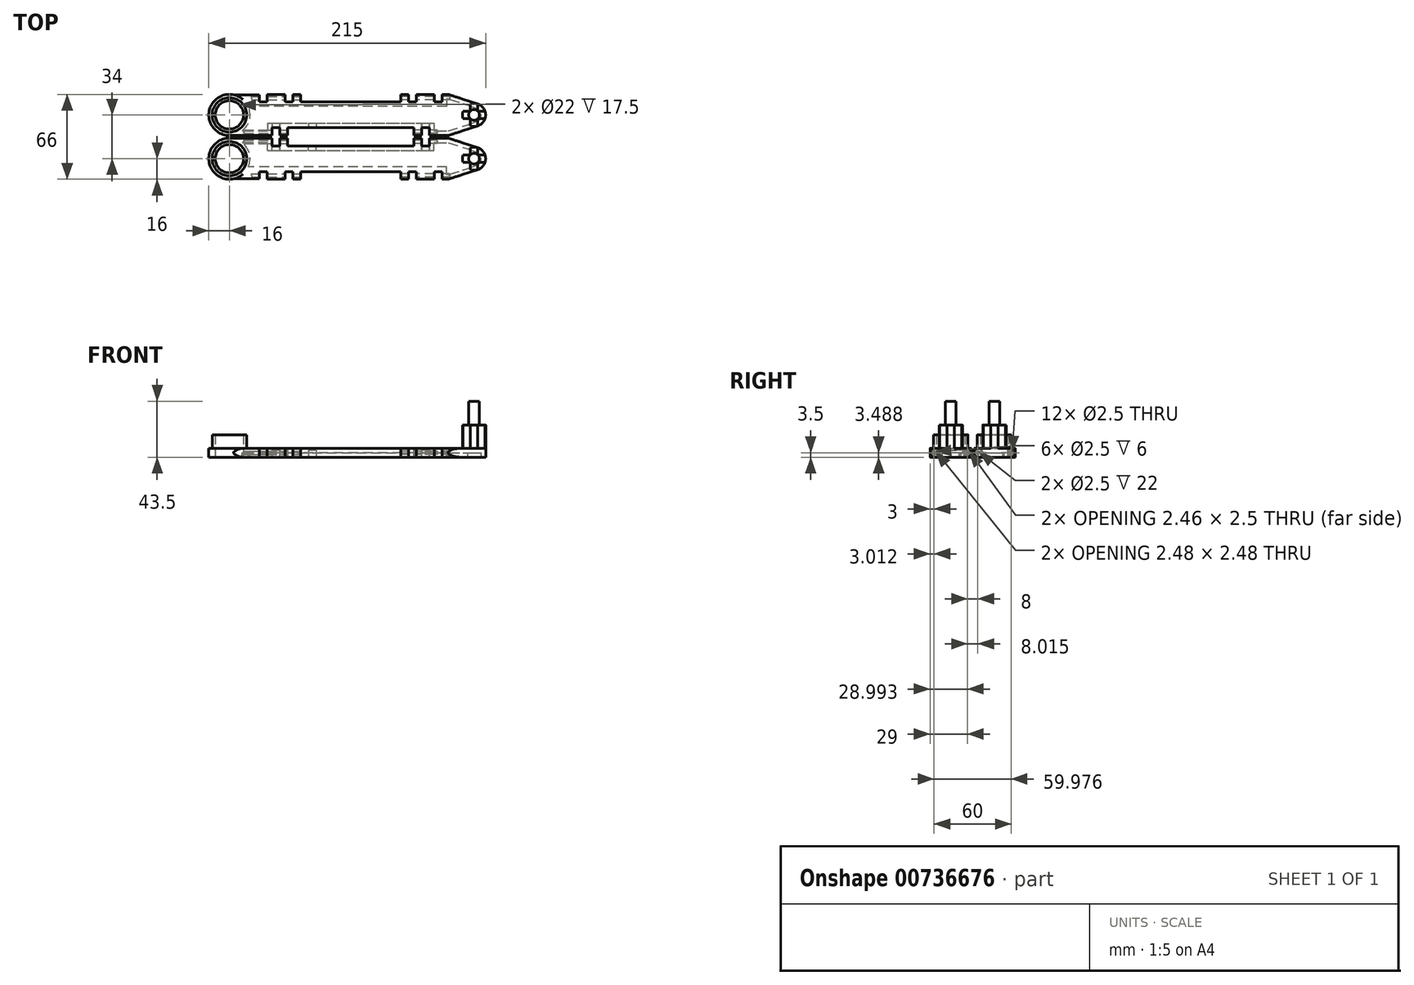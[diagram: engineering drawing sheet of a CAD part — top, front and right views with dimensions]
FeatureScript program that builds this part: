
annotation { "Feature Type Name" : "Feature", "Feature Type Description" : "" }
export const myFeature = defineFeature(function(context is Context, id is Id, definition is map)
    precondition{}
    {
        {
            var Q0;
            Q0=qCreatedBy(makeId("Top.planeOp"),FACE);
            var sketch = newSketch(context, id + "F0", { "sketchPlane" : qUnion([Q0])});
            skCircle(sketch, "E0", {"center": v(-95, 0) * mm, "radius": 11 * mm});
            skCircle(sketch, "E1", {"center": v(95, 0) * mm, "radius": 4.15 * mm});
            skCircle(sketch, "E2", {"center": v(95, 0) * mm, "radius": 9 * mm});
            skCircle(sketch, "E3", {"center": v(-95, 0) * mm, "radius": 16 * mm});
            skLineSegment(sketch, "E4.top", {"start": v(-71.75, 10) * mm, "end": v(-65.75, 10) * mm});
            skLineSegment(sketch, "E4.left", {"start": v(-71.75, 15.67) * mm, "end": v(-71.75, 10) * mm});
            skLineSegment(sketch, "E4.right", {"start": v(-65.75, 16) * mm, "end": v(-65.75, 10) * mm});
            skLineSegment(sketch, "E5.top", {"start": v(-51.75, 10) * mm, "end": v(-45.75, 10) * mm});
            skLineSegment(sketch, "E5.left", {"start": v(-51.75, 16) * mm, "end": v(-51.75, 10) * mm});
            skLineSegment(sketch, "E5.right", {"start": v(-45.75, 16) * mm, "end": v(-45.75, 10) * mm});
            skLineSegment(sketch, "E6.bottom", {"start": v(50.25, 16) * mm, "end": v(64.25, 16) * mm});
            skLineSegment(sketch, "E6.left", {"start": v(50.25, 16) * mm, "end": v(50.25, 10) * mm});
            skLineSegment(sketch, "E6.right", {"start": v(64.25, 16) * mm, "end": v(64.25, 10) * mm});
            skLineSegment(sketch, "E7.bottom", {"start": v(70.25, 16) * mm, "end": v(75, 16) * mm});
            skLineSegment(sketch, "E7.left", {"start": v(70.25, 16) * mm, "end": v(70.25, 10) * mm});
            skLineSegment(sketch, "E8.right", {"start": v(60.25, -16) * mm, "end": v(60.25, -10) * mm});
            skLineSegment(sketch, "E9.bottom", {"start": v(54.25, -16) * mm, "end": v(48.25, -16) * mm});
            skLineSegment(sketch, "E9.left", {"start": v(54.25, -16) * mm, "end": v(54.25, -10) * mm});
            skLineSegment(sketch, "E9.right", {"start": v(48.25, -16) * mm, "end": v(48.25, -10) * mm});
            skLineSegment(sketch, "E10.top", {"start": v(-61.75, -10) * mm, "end": v(-55.75, -10) * mm});
            skLineSegment(sketch, "E10.left", {"start": v(-61.75, -16) * mm, "end": v(-61.75, -10) * mm});
            skLineSegment(sketch, "E10.right", {"start": v(-55.75, -16) * mm, "end": v(-55.75, -10) * mm});
            skLineSegment(sketch, "E11.top", {"start": v(-49.75, -10) * mm, "end": v(-43.75, -10) * mm});
            skLineSegment(sketch, "E11.left", {"start": v(-49.75, -16) * mm, "end": v(-49.75, -10) * mm});
            skLineSegment(sketch, "E12", {"start": v(-43.75, -10) * mm, "end": v(48.25, -10) * mm});
            skLineSegment(sketch, "E13.top", {"start": v(-39.75, 10) * mm, "end": v(-33.75, 10) * mm});
            skLineSegment(sketch, "E13.left", {"start": v(-39.75, 16) * mm, "end": v(-39.75, 10) * mm});
            skLineSegment(sketch, "E14.bottom", {"start": v(38.25, 16) * mm, "end": v(44.25, 16) * mm});
            skLineSegment(sketch, "E14.left", {"start": v(38.25, 16) * mm, "end": v(38.25, 10) * mm});
            skLineSegment(sketch, "E14.right", {"start": v(44.25, 16) * mm, "end": v(44.25, 10) * mm});
            skLineSegment(sketch, "E15", {"start": v(-33.75, 10) * mm, "end": v(38.25, 10) * mm});
            skLineSegment(sketch, "E16", {"start": v(44.25, 10) * mm, "end": v(50.25, 10) * mm});
            skLineSegment(sketch, "E17", {"start": v(64.25, 10) * mm, "end": v(70.25, 10) * mm});
            skLineSegment(sketch, "E18", {"start": v(54.25, -10) * mm, "end": v(60.25, -10) * mm});
            skLineSegment(sketch, "E19", {"start": v(-71.75, 15.67) * mm, "end": v(-91.75, 15.67) * mm});
            skLineSegment(sketch, "E20", {"start": v(-61.75, -16) * mm, "end": v(-95, -16) * mm});
            skLineSegment(sketch, "E21", {"start": v(-55.75, -16) * mm, "end": v(-49.75, -16) * mm});
            skLineSegment(sketch, "E22", {"start": v(-65.75, 16) * mm, "end": v(-51.75, 16) * mm});
            skLineSegment(sketch, "E23", {"start": v(-45.75, 16) * mm, "end": v(-39.75, 16) * mm});
            skLineSegment(sketch, "E24", {"start": v(75, 16) * mm, "end": v(97.8, 8.56) * mm});
            skLineSegment(sketch, "E25", {"start": v(60.25, -16) * mm, "end": v(75, -16) * mm});
            skLineSegment(sketch, "E26", {"start": v(75, -16) * mm, "end": v(97.8, -8.56) * mm});
            skLineSegment(sketch, "E27", {"start": v(92.06, 2.92) * mm, "end": v(92.06, 8.5) * mm});
            skLineSegment(sketch, "E28", {"start": v(97.94, 2.92) * mm, "end": v(97.94, 8.5) * mm});
            skLineSegment(sketch, "E29", {"start": v(97.94, 2.92) * mm, "end": v(103.51, 2.92) * mm});
            skLineSegment(sketch, "E30", {"start": v(97.94, -2.93) * mm, "end": v(103.51, -2.93) * mm});
            skLineSegment(sketch, "E31", {"start": v(97.94, -2.93) * mm, "end": v(97.94, -8.5) * mm});
            skLineSegment(sketch, "E32", {"start": v(92.06, -2.93) * mm, "end": v(92.06, -8.5) * mm});
            skLineSegment(sketch, "E33", {"start": v(92.06, -2.93) * mm, "end": v(86.49, -2.93) * mm});
            skLineSegment(sketch, "E34", {"start": v(92.06, 2.92) * mm, "end": v(86.49, 2.92) * mm});
            skLineSegment(sketch, "E35", {"start": v(-65.25, -6.5) * mm, "end": v(-65.25, -12.5) * mm});
            skLineSegment(sketch, "E36", {"start": v(-65.25, -12.5) * mm, "end": v(-85.01, -12.5) * mm});
            skLineSegment(sketch, "E37", {"start": v(-65.25, -6.5) * mm, "end": v(63.75, -6.5) * mm});
            skLineSegment(sketch, "E38", {"start": v(63.75, -6.5) * mm, "end": v(63.75, -12.5) * mm});
            skLineSegment(sketch, "E39", {"start": v(63.75, -12.5) * mm, "end": v(75, -12.5) * mm});
            skLineSegment(sketch, "E40", {"start": v(73.75, 12.5) * mm, "end": v(75, 12.5) * mm});
            skLineSegment(sketch, "E41", {"start": v(75, 12.5) * mm, "end": v(90.12, 7.56) * mm});
            skLineSegment(sketch, "E42", {"start": v(73.75, 12.5) * mm, "end": v(73.75, 6.5) * mm});
            skLineSegment(sketch, "E43", {"start": v(73.75, 6.5) * mm, "end": v(-80.38, 6.5) * mm});
            skLineSegment(sketch, "E44", {"start": v(75, -12.5) * mm, "end": v(90.12, -7.56) * mm});
            skLineSegment(sketch, "E45", {"start": v(104, 0) * mm, "end": v(86, 0) * mm, "construction": true});
            skCircle(sketch, "E46", {"center": v(95, 0) * mm, "radius": 5.5 * mm});
            skLineSegment(sketch, "E47", {"start": v(90.12, -7.56) * mm, "end": v(96.84, -5.18) * mm});
            skLineSegment(sketch, "E48", {"start": v(90.12, 7.56) * mm, "end": v(96.84, 5.18) * mm});
            skLineSegment(sketch, "E49.bottom", {"start": v(-39.75, -10) * mm, "end": v(-33.75, -10) * mm});
            skLineSegment(sketch, "E49.top", {"start": v(-39.75, -16) * mm, "end": v(-33.75, -16) * mm});
            skLineSegment(sketch, "E49.left", {"start": v(-39.75, -10) * mm, "end": v(-39.75, -16) * mm});
            skLineSegment(sketch, "E49.right", {"start": v(-33.75, -10) * mm, "end": v(-33.75, -16) * mm});
            skLineSegment(sketch, "E50.bottom", {"start": v(-27.75, -10) * mm, "end": v(-21.75, -10) * mm});
            skLineSegment(sketch, "E50.top", {"start": v(-27.75, -16) * mm, "end": v(-21.75, -16) * mm});
            skLineSegment(sketch, "E50.left", {"start": v(-27.75, -10) * mm, "end": v(-27.75, -16) * mm});
            skLineSegment(sketch, "E50.right", {"start": v(-21.75, -10) * mm, "end": v(-21.75, -16) * mm});
            skCircle(sketch, "E51", {"center": v(-95, 0) * mm, "radius": 13.4 * mm});
            skSolve(sketch);
        }
        {
            var Q0;
            Q0=makeQuery(id+"F0.imprint","IMPRINT",FACE,{"disambiguationData":[TD([[makeQuery(id+"F0.imprint","IMPRINT",EDGE,{"derivedFrom":sQuery(id+"F0.wireOp",EDGE,"E4.top")}),-1.0]])]});
            var Q1;
            Q1=makeQuery(id+"F0.imprint","IMPRINT",FACE,{"disambiguationData":[TD([[makeQuery(id+"F0.imprint","IMPRINT",EDGE,{"derivedFrom":sQuery(id+"F0.wireOp",EDGE,"E0")}),-1.0]])]});
            var Q2;
            {var subQ0=sQuery(id+"F0.wireOp",EDGE,"u77ph5UG-GRJr-q7rl-wOkM-NqZfjSpqDGZQ");var subQ1=sQuery(id+"F0.wireOp",EDGE,"E1");var subQ2=makeQuery(id+"F0.imprint","INTERSECT",VERTEX,{"disambiguationData":[OD(0.0)],"derivedFrom":[subQ1,subQ0]});Q2=makeQuery(id+"F0.imprint","IMPRINT",FACE,{"disambiguationData":[TD([[makeQuery(id+"F0.imprint","IMPRINT",EDGE,{"disambiguationData":[TD([[subQ2,-1.0]])],"derivedFrom":subQ1}),-1.0]])]});}
            var Q3;
            {var subQ0=sQuery(id+"F0.wireOp",EDGE,"u77ph5UG-GRJr-q7rl-wOkM-NqZfjSpqDGZQ");var subQ1=sQuery(id+"F0.wireOp",EDGE,"E1");var subQ2=makeQuery(id+"F0.imprint","INTERSECT",VERTEX,{"disambiguationData":[OD(0.0)],"derivedFrom":[subQ1,subQ0]});Q3=makeQuery(id+"F0.imprint","IMPRINT",FACE,{"disambiguationData":[TD([[makeQuery(id+"F0.imprint","IMPRINT",EDGE,{"disambiguationData":[TD([[subQ2,-1.0]])],"derivedFrom":subQ1}),1.0]])]});}
            var Q4;
            {var subQ0=sQuery(id+"F0.wireOp",EDGE,"u77ph5UG-GRJr-q7rl-wOkM-NqZfjSpqDGZQ");var subQ1=sQuery(id+"F0.wireOp",EDGE,"E1");var subQ2=makeQuery(id+"F0.imprint","INTERSECT",VERTEX,{"disambiguationData":[OD(0.0)],"derivedFrom":[subQ1,subQ0]});Q4=makeQuery(id+"F0.imprint","IMPRINT",FACE,{"disambiguationData":[TD([[makeQuery(id+"F0.imprint","IMPRINT",EDGE,{"disambiguationData":[TD([[subQ2,1.0]])],"derivedFrom":subQ1}),1.0]])]});}
            var Q5;
            {var subQ0=sQuery(id+"F0.wireOp",EDGE,"u77ph5UG-GRJr-q7rl-wOkM-NqZfjSpqDGZQ");var subQ1=sQuery(id+"F0.wireOp",EDGE,"E1");var subQ2=makeQuery(id+"F0.imprint","INTERSECT",VERTEX,{"disambiguationData":[OD(0.0)],"derivedFrom":[subQ1,subQ0]});Q5=makeQuery(id+"F0.imprint","IMPRINT",FACE,{"disambiguationData":[TD([[makeQuery(id+"F0.imprint","IMPRINT",EDGE,{"disambiguationData":[TD([[subQ2,1.0]])],"derivedFrom":subQ1}),-1.0]])]});}
            var Q6;
            Q6=makeQuery(id+"F0.imprint","IMPRINT",FACE,{"disambiguationData":[TD([[makeQuery(id+"F0.imprint","IMPRINT",EDGE,{"derivedFrom":sQuery(id+"F0.wireOp",EDGE,"E8.right")}),-1.0]])]});
            var Q7;
            {var subQ2=sQuery(id+"F0.wireOp",EDGE,"E31");Q7=makeQuery(id+"F0.imprint","IMPRINT",FACE,{"disambiguationData":[TD([[makeQuery(id+"F0.imprint","IMPRINT",EDGE,{"derivedFrom":subQ2}),-1.0]])]});}
            var Q8;
            {var subQ3=sQuery(id+"F0.wireOp",EDGE,"E32");Q8=makeQuery(id+"F0.imprint","IMPRINT",FACE,{"disambiguationData":[TD([[makeQuery(id+"F0.imprint","IMPRINT",EDGE,{"derivedFrom":subQ3}),-1.0]])]});}
            var Q9;
            {var subQ0=sQuery(id+"F0.wireOp",EDGE,"E30");Q9=makeQuery(id+"F0.imprint","IMPRINT",FACE,{"disambiguationData":[TD([[makeQuery(id+"F0.imprint","IMPRINT",EDGE,{"derivedFrom":subQ0}),-1.0]])]});}
            var Q10;
            {var subQ0=sQuery(id+"F0.wireOp",EDGE,"E28");Q10=makeQuery(id+"F0.imprint","IMPRINT",FACE,{"disambiguationData":[TD([[makeQuery(id+"F0.imprint","IMPRINT",EDGE,{"derivedFrom":subQ0}),-1.0]])]});}
            var Q11;
            {var subQ0=sQuery(id+"F0.wireOp",EDGE,"E27");Q11=makeQuery(id+"F0.imprint","IMPRINT",FACE,{"disambiguationData":[TD([[makeQuery(id+"F0.imprint","IMPRINT",EDGE,{"derivedFrom":subQ0}),-1.0]])]});}
            var Q12;
            {var subQ0=sQuery(id+"F0.wireOp",EDGE,"E27");Q12=makeQuery(id+"F0.imprint","IMPRINT",FACE,{"disambiguationData":[TD([[makeQuery(id+"F0.imprint","IMPRINT",EDGE,{"derivedFrom":subQ0}),1.0]])]});}
            var Q13;
            {var subQ0=sQuery(id+"F0.wireOp",EDGE,"E33");Q13=makeQuery(id+"F0.imprint","IMPRINT",FACE,{"disambiguationData":[TD([[makeQuery(id+"F0.imprint","IMPRINT",EDGE,{"derivedFrom":subQ0}),1.0]])]});}
            var Q14;
            {var subQ0=sQuery(id+"F0.wireOp",EDGE,"E34");Q14=makeQuery(id+"F0.imprint","IMPRINT",FACE,{"disambiguationData":[TD([[makeQuery(id+"F0.imprint","IMPRINT",EDGE,{"derivedFrom":subQ0}),-1.0]])]});}
            var Q15;
            {var subQ0=sQuery(id+"F0.wireOp",EDGE,"E46");var subQ1=sQuery(id+"F0.wireOp",EDGE,"E27");var subQ2=makeQuery(id+"F0.imprint","INTERSECT",VERTEX,{"derivedFrom":[subQ1,subQ0]});Q15=makeQuery(id+"F0.imprint","IMPRINT",FACE,{"disambiguationData":[TD([[makeQuery(id+"F0.imprint","IMPRINT",EDGE,{"disambiguationData":[TD([[subQ2,-1.0]])],"derivedFrom":subQ1}),1.0]])]});}
            var Q16;
            {var subQ0=sQuery(id+"F0.wireOp",EDGE,"E46");var subQ1=makeQuery(id+"F0.imprint","INTERSECT",VERTEX,{"derivedFrom":[subQ0,sQuery(id+"F0.wireOp",EDGE,"E48")]});Q16=makeQuery(id+"F0.imprint","IMPRINT",FACE,{"disambiguationData":[TD([[makeQuery(id+"F0.imprint","IMPRINT",EDGE,{"disambiguationData":[TD([[subQ1,1.0]])],"derivedFrom":subQ0}),1.0]])]});}
            var Q17;
            {var subQ1=sQuery(id+"F0.wireOp",EDGE,"E2");var subQ5=makeQuery(id+"F0.imprint","INTERSECT",VERTEX,{"derivedFrom":[subQ1,sQuery(id+"F0.wireOp",EDGE,"E24")]});Q17=makeQuery(id+"F0.imprint","IMPRINT",FACE,{"disambiguationData":[TD([[makeQuery(id+"F0.imprint","IMPRINT",EDGE,{"disambiguationData":[TD([[subQ5,1.0]])],"derivedFrom":subQ1}),1.0]])]});}
            var Q18;
            {var subQ0=sQuery(id+"F0.wireOp",EDGE,"E28");var subQ1=sQuery(id+"F0.wireOp",EDGE,"E2");var subQ2=makeQuery(id+"F0.imprint","INTERSECT",VERTEX,{"derivedFrom":[subQ1,subQ0]});Q18=makeQuery(id+"F0.imprint","IMPRINT",FACE,{"disambiguationData":[TD([[makeQuery(id+"F0.imprint","IMPRINT",EDGE,{"disambiguationData":[TD([[subQ2,1.0]])],"derivedFrom":subQ1}),1.0]])]});}
            var Q19;
            {var subQ0=sQuery(id+"F0.wireOp",EDGE,"E30");var subQ1=sQuery(id+"F0.wireOp",EDGE,"E2");var subQ2=makeQuery(id+"F0.imprint","INTERSECT",VERTEX,{"derivedFrom":[subQ1,subQ0]});Q19=makeQuery(id+"F0.imprint","IMPRINT",FACE,{"disambiguationData":[TD([[makeQuery(id+"F0.imprint","IMPRINT",EDGE,{"disambiguationData":[TD([[subQ2,1.0]])],"derivedFrom":subQ1}),1.0]])]});}
            var Q20;
            {var subQ1=sQuery(id+"F0.wireOp",EDGE,"E2");var subQ9=makeQuery(id+"F0.imprint","INTERSECT",VERTEX,{"derivedFrom":[subQ1,sQuery(id+"F0.wireOp",EDGE,"E26")]});Q20=makeQuery(id+"F0.imprint","IMPRINT",FACE,{"disambiguationData":[TD([[makeQuery(id+"F0.imprint","IMPRINT",EDGE,{"disambiguationData":[TD([[subQ9,1.0]])],"derivedFrom":subQ1}),1.0]])]});}
            var Q21;
            {var subQ0=sQuery(id+"F0.wireOp",EDGE,"E46");var subQ1=sQuery(id+"F0.wireOp",EDGE,"E32");var subQ2=makeQuery(id+"F0.imprint","INTERSECT",VERTEX,{"derivedFrom":[subQ1,subQ0]});Q21=makeQuery(id+"F0.imprint","IMPRINT",FACE,{"disambiguationData":[TD([[makeQuery(id+"F0.imprint","IMPRINT",EDGE,{"disambiguationData":[TD([[subQ2,-1.0]])],"derivedFrom":subQ1}),-1.0]])]});}
            var Q22;
            {var subQ0=sQuery(id+"F0.wireOp",EDGE,"E46");var subQ1=sQuery(id+"F0.wireOp",EDGE,"E32");var subQ2=makeQuery(id+"F0.imprint","INTERSECT",VERTEX,{"derivedFrom":[subQ1,subQ0]});Q22=makeQuery(id+"F0.imprint","IMPRINT",FACE,{"disambiguationData":[TD([[makeQuery(id+"F0.imprint","IMPRINT",EDGE,{"disambiguationData":[TD([[subQ2,-1.0]])],"derivedFrom":subQ1}),1.0]])]});}
            var Q23;
            Q23=makeQuery(id+"F0.imprint","IMPRINT",FACE,{"disambiguationData":[TD([[makeQuery(id+"F0.imprint","IMPRINT",EDGE,{"derivedFrom":sQuery(id+"F0.wireOp",EDGE,"E35")}),-1.0]])]});
            var Q24;
            {var subQ0=sQuery(id+"F0.wireOp",EDGE,"E33");var subQ1=sQuery(id+"F0.wireOp",EDGE,"E2");var subQ2=makeQuery(id+"F0.imprint","INTERSECT",VERTEX,{"derivedFrom":[subQ1,subQ0]});Q24=makeQuery(id+"F0.imprint","IMPRINT",FACE,{"disambiguationData":[TD([[makeQuery(id+"F0.imprint","IMPRINT",EDGE,{"disambiguationData":[TD([[subQ2,1.0]])],"derivedFrom":subQ1}),1.0]])]});}
            var Q25;
            {var subQ0=sQuery(id+"F0.wireOp",EDGE,"E29");var subQ1=sQuery(id+"F0.wireOp",EDGE,"E2");var subQ2=makeQuery(id+"F0.imprint","INTERSECT",VERTEX,{"derivedFrom":[subQ1,subQ0]});Q25=makeQuery(id+"F0.imprint","IMPRINT",FACE,{"disambiguationData":[TD([[makeQuery(id+"F0.imprint","IMPRINT",EDGE,{"disambiguationData":[TD([[subQ2,1.0]])],"derivedFrom":subQ1}),1.0]])]});}
            var Q26;
            {var subQ0=sQuery(id+"F0.wireOp",EDGE,"XVzFhhWt-0BN3-hWAi-U9tN-sKV1pTIN5wL4");Q26=makeQuery(id+"F0.imprint","IMPRINT",FACE,{"disambiguationData":[TD([[makeQuery(id+"F0.imprint","IMPRINT",EDGE,{"derivedFrom":subQ0}),1.0]])]});}
            var Q27;
            Q27=makeQuery(id+"F0.imprint","IMPRINT",FACE,{"disambiguationData":[TD([[makeQuery(id+"F0.imprint","IMPRINT",EDGE,{"derivedFrom":sQuery(id+"F0.wireOp",EDGE,"mNT0CxhN-jVKA-UhMB-i0di-VQKrBtZCWN2a.bottom")}),1.0]])]});
            var Q28;
            Q28=makeQuery(id+"F0.imprint","IMPRINT",FACE,{"disambiguationData":[TD([[makeQuery(id+"F0.imprint","IMPRINT",EDGE,{"derivedFrom":sQuery(id+"F0.wireOp",EDGE,"G2ZhGwMG-Es2m-OFSZ-C1h7-AwqjGMnpP9Lz.bottom")}),1.0]])]});
            var Q29;
            Q29=makeQuery(id+"F0.imprint","IMPRINT",FACE,{"disambiguationData":[TD([[makeQuery(id+"F0.imprint","IMPRINT",EDGE,{"derivedFrom":sQuery(id+"F0.wireOp",EDGE,"E49.bottom")}),-1.0]])]});
            var Q30;
            Q30=makeQuery(id+"F0.imprint","IMPRINT",FACE,{"disambiguationData":[TD([[makeQuery(id+"F0.imprint","IMPRINT",EDGE,{"derivedFrom":sQuery(id+"F0.wireOp",EDGE,"E50.bottom")}),-1.0]])]});
            var Q31;
            Q31=makeQuery(id+"F0.imprint","IMPRINT",FACE,{"disambiguationData":[TD([[makeQuery(id+"F0.imprint","IMPRINT",EDGE,{"derivedFrom":sQuery(id+"F0.wireOp",EDGE,"E51")}),-1.0]])]});
            extrude(context, id + "F1", {"entities" : qUnion([Q0, Q1, Q2, Q3, Q4, Q5, Q6, Q7, Q8, Q9, Q10, Q11, Q12, Q13, Q14, Q15, Q16, Q17, Q18, Q19, Q20, Q21, Q22, Q23, Q24, Q25, Q26, Q27, Q28, Q29, Q30, Q31]), "depth" : 3.5 * mm, "offsetDistance" : 25 * mm});
        }
        {
            var Q0;
            Q0=makeQuery(id+"F0.imprint","IMPRINT",FACE,{"disambiguationData":[TD([[makeQuery(id+"F0.imprint","IMPRINT",EDGE,{"derivedFrom":sQuery(id+"F0.wireOp",EDGE,"E1")}),1.0]])]});
            var Q1;
            Q1=makeQuery(id+"F0.imprint","IMPRINT",FACE,{"disambiguationData":[TD([[makeQuery(id+"F0.imprint","IMPRINT",EDGE,{"derivedFrom":sQuery(id+"F0.wireOp",EDGE,"E1")}),-1.0]])]});
            var Q2;
            {var subQ0=sQuery(id+"F0.wireOp",EDGE,"E27");Q2=makeQuery(id+"F0.imprint","IMPRINT",FACE,{"disambiguationData":[TD([[makeQuery(id+"F0.imprint","IMPRINT",EDGE,{"derivedFrom":subQ0}),-1.0]])]});}
            var Q3;
            {var subQ2=sQuery(id+"F0.wireOp",EDGE,"E31");Q3=makeQuery(id+"F0.imprint","IMPRINT",FACE,{"disambiguationData":[TD([[makeQuery(id+"F0.imprint","IMPRINT",EDGE,{"derivedFrom":subQ2}),-1.0]])]});}
            var Q4;
            {var subQ1=sQuery(id+"F0.wireOp",EDGE,"E2");var subQ5=makeQuery(id+"F0.imprint","INTERSECT",VERTEX,{"derivedFrom":[subQ1,sQuery(id+"F0.wireOp",EDGE,"E24")]});Q4=makeQuery(id+"F0.imprint","IMPRINT",FACE,{"disambiguationData":[TD([[makeQuery(id+"F0.imprint","IMPRINT",EDGE,{"disambiguationData":[TD([[subQ5,1.0]])],"derivedFrom":subQ1}),1.0]])]});}
            var Q5;
            {var subQ1=sQuery(id+"F0.wireOp",EDGE,"E2");var subQ9=makeQuery(id+"F0.imprint","INTERSECT",VERTEX,{"derivedFrom":[subQ1,sQuery(id+"F0.wireOp",EDGE,"E26")]});Q5=makeQuery(id+"F0.imprint","IMPRINT",FACE,{"disambiguationData":[TD([[makeQuery(id+"F0.imprint","IMPRINT",EDGE,{"disambiguationData":[TD([[subQ9,1.0]])],"derivedFrom":subQ1}),1.0]])]});}
            var Q6;
            {var subQ0=sQuery(id+"F0.wireOp",EDGE,"E46");var subQ1=sQuery(id+"F0.wireOp",EDGE,"E32");var subQ2=makeQuery(id+"F0.imprint","INTERSECT",VERTEX,{"derivedFrom":[subQ1,subQ0]});Q6=makeQuery(id+"F0.imprint","IMPRINT",FACE,{"disambiguationData":[TD([[makeQuery(id+"F0.imprint","IMPRINT",EDGE,{"disambiguationData":[TD([[subQ2,-1.0]])],"derivedFrom":subQ1}),1.0]])]});}
            var Q7;
            {var subQ0=sQuery(id+"F0.wireOp",EDGE,"E33");var subQ1=sQuery(id+"F0.wireOp",EDGE,"E2");var subQ2=makeQuery(id+"F0.imprint","INTERSECT",VERTEX,{"derivedFrom":[subQ1,subQ0]});Q7=makeQuery(id+"F0.imprint","IMPRINT",FACE,{"disambiguationData":[TD([[makeQuery(id+"F0.imprint","IMPRINT",EDGE,{"disambiguationData":[TD([[subQ2,1.0]])],"derivedFrom":subQ1}),1.0]])]});}
            var Q8;
            {var subQ0=sQuery(id+"F0.wireOp",EDGE,"E29");var subQ1=sQuery(id+"F0.wireOp",EDGE,"E2");var subQ2=makeQuery(id+"F0.imprint","INTERSECT",VERTEX,{"derivedFrom":[subQ1,subQ0]});Q8=makeQuery(id+"F0.imprint","IMPRINT",FACE,{"disambiguationData":[TD([[makeQuery(id+"F0.imprint","IMPRINT",EDGE,{"disambiguationData":[TD([[subQ2,1.0]])],"derivedFrom":subQ1}),1.0]])]});}
            var Q9;
            {var subQ0=sQuery(id+"F0.wireOp",EDGE,"E46");var subQ1=makeQuery(id+"F0.imprint","INTERSECT",VERTEX,{"derivedFrom":[subQ0,sQuery(id+"F0.wireOp",EDGE,"E48")]});Q9=makeQuery(id+"F0.imprint","IMPRINT",FACE,{"disambiguationData":[TD([[makeQuery(id+"F0.imprint","IMPRINT",EDGE,{"disambiguationData":[TD([[subQ1,1.0]])],"derivedFrom":subQ0}),1.0]])]});}
            extrude(context, id + "F2", {"entities" : qUnion([Q0, Q1, Q2, Q3, Q4, Q5, Q6, Q7, Q8, Q9]), "operationType" : NewBodyOperationType.ADD, "depth" : 21.5 * mm, "offsetDistance" : 25 * mm});
        }
        {
            var Q0;
            Q0=makeQuery(id+"F0.imprint","IMPRINT",FACE,{"disambiguationData":[TD([[makeQuery(id+"F0.imprint","IMPRINT",EDGE,{"derivedFrom":sQuery(id+"F0.wireOp",EDGE,"E1")}),1.0]])]});
            extrude(context, id + "F3", {"entities" : qUnion([Q0]), "operationType" : NewBodyOperationType.ADD, "depth" : 40 * mm, "offsetDistance" : 25 * mm});
        }
        {
            var Q0;
            Q0=makeQuery(id+"F0.imprint","IMPRINT",FACE,{"disambiguationData":[TD([[makeQuery(id+"F0.imprint","IMPRINT",EDGE,{"derivedFrom":sQuery(id+"F0.wireOp",EDGE,"E4.top")}),-1.0]])]});
            var Q1;
            Q1=makeQuery(id+"F0.imprint","IMPRINT",FACE,{"disambiguationData":[TD([[makeQuery(id+"F0.imprint","IMPRINT",EDGE,{"derivedFrom":sQuery(id+"F0.wireOp",EDGE,"E8.right")}),-1.0]])]});
            var Q2;
            Q2=makeQuery(id+"F0.imprint","IMPRINT",FACE,{"disambiguationData":[TD([[makeQuery(id+"F0.imprint","IMPRINT",EDGE,{"derivedFrom":sQuery(id+"F0.wireOp",EDGE,"E0")}),-1.0]])]});
            var Q3;
            {var subQ3=sQuery(id+"F0.wireOp",EDGE,"GdLCJ8ow-4YD3-uBdU-tEqE-DGwQXOaLyxA5");Q3=makeQuery(id+"F0.imprint","IMPRINT",FACE,{"disambiguationData":[TD([[makeQuery(id+"F0.imprint","IMPRINT",EDGE,{"derivedFrom":subQ3}),-1.0]])]});}
            var Q4;
            {var subQ3=sQuery(id+"F0.wireOp",EDGE,"6zzm194w-3L6F-z26w-p0nv-BLiALKh9J1Ov");Q4=makeQuery(id+"F0.imprint","IMPRINT",FACE,{"disambiguationData":[TD([[makeQuery(id+"F0.imprint","IMPRINT",EDGE,{"derivedFrom":subQ3}),1.0]])]});}
            var Q5;
            {var subQ0=sQuery(id+"F0.wireOp",EDGE,"E30");var subQ1=sQuery(id+"F0.wireOp",EDGE,"E2");var subQ2=makeQuery(id+"F0.imprint","INTERSECT",VERTEX,{"derivedFrom":[subQ1,subQ0]});Q5=makeQuery(id+"F0.imprint","IMPRINT",FACE,{"disambiguationData":[TD([[makeQuery(id+"F0.imprint","IMPRINT",EDGE,{"disambiguationData":[TD([[subQ2,1.0]])],"derivedFrom":subQ1}),1.0]])]});}
            var Q6;
            {var subQ1=sQuery(id+"F0.wireOp",EDGE,"E2");var subQ9=makeQuery(id+"F0.imprint","INTERSECT",VERTEX,{"derivedFrom":[subQ1,sQuery(id+"F0.wireOp",EDGE,"E26")]});Q6=makeQuery(id+"F0.imprint","IMPRINT",FACE,{"disambiguationData":[TD([[makeQuery(id+"F0.imprint","IMPRINT",EDGE,{"disambiguationData":[TD([[subQ9,1.0]])],"derivedFrom":subQ1}),1.0]])]});}
            var Q7;
            {var subQ0=sQuery(id+"F0.wireOp",EDGE,"E32");var subQ1=sQuery(id+"F0.wireOp",EDGE,"E2");var subQ2=makeQuery(id+"F0.imprint","INTERSECT",VERTEX,{"derivedFrom":[subQ1,subQ0]});Q7=makeQuery(id+"F0.imprint","IMPRINT",FACE,{"disambiguationData":[TD([[makeQuery(id+"F0.imprint","IMPRINT",EDGE,{"disambiguationData":[TD([[subQ2,1.0]])],"derivedFrom":subQ0}),-1.0]])]});}
            var Q8;
            {var subQ0=sQuery(id+"F0.wireOp",EDGE,"E28");var subQ1=sQuery(id+"F0.wireOp",EDGE,"E2");var subQ2=makeQuery(id+"F0.imprint","INTERSECT",VERTEX,{"derivedFrom":[subQ1,subQ0]});Q8=makeQuery(id+"F0.imprint","IMPRINT",FACE,{"disambiguationData":[TD([[makeQuery(id+"F0.imprint","IMPRINT",EDGE,{"disambiguationData":[TD([[subQ2,1.0]])],"derivedFrom":subQ1}),1.0]])]});}
            var Q9;
            {var subQ1=sQuery(id+"F0.wireOp",EDGE,"E2");var subQ5=makeQuery(id+"F0.imprint","INTERSECT",VERTEX,{"derivedFrom":[subQ1,sQuery(id+"F0.wireOp",EDGE,"E24")]});Q9=makeQuery(id+"F0.imprint","IMPRINT",FACE,{"disambiguationData":[TD([[makeQuery(id+"F0.imprint","IMPRINT",EDGE,{"disambiguationData":[TD([[subQ5,1.0]])],"derivedFrom":subQ1}),1.0]])]});}
            var Q10;
            {var subQ0=sQuery(id+"F0.wireOp",EDGE,"E29");var subQ1=sQuery(id+"F0.wireOp",EDGE,"E2");var subQ2=makeQuery(id+"F0.imprint","INTERSECT",VERTEX,{"derivedFrom":[subQ1,subQ0]});Q10=makeQuery(id+"F0.imprint","IMPRINT",FACE,{"disambiguationData":[TD([[makeQuery(id+"F0.imprint","IMPRINT",EDGE,{"disambiguationData":[TD([[subQ2,1.0]])],"derivedFrom":subQ1}),1.0]])]});}
            var Q11;
            {var subQ0=sQuery(id+"F0.wireOp",EDGE,"E27");var subQ1=sQuery(id+"F0.wireOp",EDGE,"E2");var subQ2=makeQuery(id+"F0.imprint","INTERSECT",VERTEX,{"derivedFrom":[subQ1,subQ0]});Q11=makeQuery(id+"F0.imprint","IMPRINT",FACE,{"disambiguationData":[TD([[makeQuery(id+"F0.imprint","IMPRINT",EDGE,{"disambiguationData":[TD([[subQ2,1.0]])],"derivedFrom":subQ0}),1.0]])]});}
            var Q12;
            Q12=makeQuery(id+"F0.imprint","IMPRINT",FACE,{"disambiguationData":[TD([[makeQuery(id+"F0.imprint","IMPRINT",EDGE,{"derivedFrom":sQuery(id+"F0.wireOp",EDGE,"E50.bottom")}),-1.0]])]});
            var Q13;
            Q13=makeQuery(id+"F0.imprint","IMPRINT",FACE,{"disambiguationData":[TD([[makeQuery(id+"F0.imprint","IMPRINT",EDGE,{"derivedFrom":sQuery(id+"F0.wireOp",EDGE,"E49.bottom")}),-1.0]])]});
            var Q14;
            Q14=makeQuery(id+"F0.imprint","IMPRINT",FACE,{"disambiguationData":[TD([[makeQuery(id+"F0.imprint","IMPRINT",EDGE,{"derivedFrom":sQuery(id+"F0.wireOp",EDGE,"E51")}),-1.0]])]});
            extrude(context, id + "F4", {"entities" : qUnion([Q0, Q1, Q2, Q3, Q4, Q5, Q6, Q7, Q8, Q9, Q10, Q11, Q12, Q13, Q14]), "operationType" : NewBodyOperationType.ADD, "oppositeDirection" : true, "depth" : 3.5 * mm, "offsetDistance" : 25 * mm});
        }
        {
            var Q0;
            {var subQ0=sQuery(id+"F0.wireOp",EDGE,"E11.left");Q0=makeQuery(id+"F4.boolean.opBoolean","MERGE",FACE,{"derivedFrom":[makeQuery(id+"F1.opExtrude","SWEPT_FACE",FACE,{"disambiguationData":[OSD([subQ0])]}),makeQuery(id+"F4.opExtrude","SWEPT_FACE",FACE,{"disambiguationData":[OSD([subQ0])]})]});}
            var sketch = newSketch(context, id + "F5", { "sketchPlane" : qUnion([Q0])});
            skCircle(sketch, "E52", {"center": v(-13, 0) * mm, "radius": 1.25 * mm});
            skPoint(sketch, "E52.centerSnap0", {"position": v(-13, -3.5) * mm});
            skPoint(sketch, "E52.centerSnap1", {"position": v(-16, 0) * mm});
            skSolve(sketch);
        }
        {
            var Q0;
            Q0=makeQuery(id+"F5.imprint","IMPRINT",FACE,{"disambiguationData":[TD([[makeQuery(id+"F5.imprint","IMPRINT",EDGE,{"derivedFrom":sQuery(id+"F5.wireOp",EDGE,"E52")}),1.0]])]});
            extrude(context, id + "F6", {"entities" : qUnion([Q0]), "operationType" : NewBodyOperationType.REMOVE, "oppositeDirection" : true, "depth" : 34 * mm, "offsetDistance" : 25 * mm});
        }
        {
            var Q0;
            Q0=makeQuery(id+"F5.imprint","IMPRINT",FACE,{"disambiguationData":[TD([[makeQuery(id+"F5.imprint","IMPRINT",EDGE,{"derivedFrom":sQuery(id+"F5.wireOp",EDGE,"E52")}),1.0]])]});
            extrude(context, id + "F7", {"entities" : qUnion([Q0]), "operationType" : NewBodyOperationType.REMOVE, "depth" : 116 * mm, "offsetDistance" : 25 * mm});
        }
        {
            var Q0;
            {var subQ0=sQuery(id+"F0.wireOp",EDGE,"E14.left");Q0=makeQuery(id+"F4.boolean.opBoolean","MERGE",FACE,{"derivedFrom":[makeQuery(id+"F1.opExtrude","SWEPT_FACE",FACE,{"disambiguationData":[OSD([subQ0])]}),makeQuery(id+"F4.opExtrude","SWEPT_FACE",FACE,{"disambiguationData":[OSD([subQ0])]})]});}
            var sketch = newSketch(context, id + "F8", { "sketchPlane" : qUnion([Q0])});
            skCircle(sketch, "E53", {"center": v(-13, 0) * mm, "radius": 1.25 * mm});
            skPoint(sketch, "E53.centerSnap0", {"position": v(-13, 3.5) * mm});
            skPoint(sketch, "E53.centerSnap1", {"position": v(-16, 0) * mm});
            skSolve(sketch);
        }
        {
            var Q0;
            Q0=makeQuery(id+"F8.imprint","IMPRINT",FACE,{"disambiguationData":[TD([[makeQuery(id+"F8.imprint","IMPRINT",EDGE,{"derivedFrom":sQuery(id+"F8.wireOp",EDGE,"E53")}),1.0]])]});
            extrude(context, id + "F9", {"entities" : qUnion([Q0]), "operationType" : NewBodyOperationType.REMOVE, "oppositeDirection" : true, "depth" : 38 * mm, "offsetDistance" : 25 * mm});
        }
        {
            var Q0;
            Q0=makeQuery(id+"F8.imprint","IMPRINT",FACE,{"disambiguationData":[TD([[makeQuery(id+"F8.imprint","IMPRINT",EDGE,{"derivedFrom":sQuery(id+"F8.wireOp",EDGE,"E53")}),1.0]])]});
            extrude(context, id + "F10", {"entities" : qUnion([Q0]), "operationType" : NewBodyOperationType.REMOVE, "depth" : 116 * mm, "offsetDistance" : 25 * mm});
        }
        {
            var Q0;
            Q0=makeQuery(id+"F1.opExtrude","CAP_EDGE",EDGE,{"disambiguationData":[OSD([sQuery(id+"F0.wireOp",EDGE,"E14.bottom")])],"isStart":false});
            var Q1;
            Q1=makeQuery(id+"F4.opExtrude","CAP_EDGE",EDGE,{"disambiguationData":[OSD([sQuery(id+"F0.wireOp",EDGE,"E14.bottom")])],"isStart":false});
            var Q2;
            Q2=makeQuery(id+"F1.opExtrude","CAP_EDGE",EDGE,{"disambiguationData":[OSD([sQuery(id+"F0.wireOp",EDGE,"E6.bottom")])],"isStart":false});
            var Q3;
            Q3=makeQuery(id+"F4.opExtrude","CAP_EDGE",EDGE,{"disambiguationData":[OSD([sQuery(id+"F0.wireOp",EDGE,"E6.bottom")])],"isStart":false});
            var Q4;
            Q4=makeQuery(id+"F1.opExtrude","CAP_EDGE",EDGE,{"disambiguationData":[OSD([sQuery(id+"F0.wireOp",EDGE,"E7.bottom")])],"isStart":false});
            var Q5;
            Q5=makeQuery(id+"F4.opExtrude","CAP_EDGE",EDGE,{"disambiguationData":[OSD([sQuery(id+"F0.wireOp",EDGE,"E7.bottom")])],"isStart":false});
            var Q6;
            Q6=makeQuery(id+"F4.opExtrude","CAP_EDGE",EDGE,{"disambiguationData":[OSD([sQuery(id+"F0.wireOp",EDGE,"E25")])],"isStart":false});
            var Q7;
            Q7=makeQuery(id+"F4.opExtrude","CAP_EDGE",EDGE,{"disambiguationData":[OSD([sQuery(id+"F0.wireOp",EDGE,"E9.bottom")])],"isStart":false});
            var Q8;
            Q8=makeQuery(id+"F4.opExtrude","CAP_EDGE",EDGE,{"disambiguationData":[OSD([sQuery(id+"F0.wireOp",EDGE,"E19")])],"isStart":false});
            var Q9;
            Q9=makeQuery(id+"F1.opExtrude","CAP_EDGE",EDGE,{"disambiguationData":[OSD([sQuery(id+"F0.wireOp",EDGE,"E19")])],"isStart":false});
            var Q10;
            Q10=makeQuery(id+"F4.opExtrude","CAP_EDGE",EDGE,{"disambiguationData":[OSD([sQuery(id+"F0.wireOp",EDGE,"E22")])],"isStart":false});
            var Q11;
            Q11=makeQuery(id+"F1.opExtrude","CAP_EDGE",EDGE,{"disambiguationData":[OSD([sQuery(id+"F0.wireOp",EDGE,"E22")])],"isStart":false});
            var Q12;
            Q12=makeQuery(id+"F4.opExtrude","CAP_EDGE",EDGE,{"disambiguationData":[OSD([sQuery(id+"F0.wireOp",EDGE,"E23")])],"isStart":false});
            var Q13;
            Q13=makeQuery(id+"F1.opExtrude","CAP_EDGE",EDGE,{"disambiguationData":[OSD([sQuery(id+"F0.wireOp",EDGE,"E23")])],"isStart":false});
            var Q14;
            Q14=makeQuery(id+"F1.opExtrude","CAP_EDGE",EDGE,{"disambiguationData":[OSD([sQuery(id+"F0.wireOp",EDGE,"E21")])],"isStart":false});
            var Q15;
            Q15=makeQuery(id+"F4.opExtrude","CAP_EDGE",EDGE,{"disambiguationData":[OSD([sQuery(id+"F0.wireOp",EDGE,"E21")])],"isStart":false});
            var Q16;
            Q16=makeQuery(id+"F1.opExtrude","CAP_EDGE",EDGE,{"disambiguationData":[OSD([sQuery(id+"F0.wireOp",EDGE,"E9.bottom")])],"isStart":false});
            var Q17;
            Q17=makeQuery(id+"F1.opExtrude","CAP_EDGE",EDGE,{"disambiguationData":[OSD([sQuery(id+"F0.wireOp",EDGE,"E25")])],"isStart":false});
            var Q18;
            Q18=makeQuery(id+"F4.opExtrude","CAP_EDGE",EDGE,{"disambiguationData":[OSD([sQuery(id+"F0.wireOp",EDGE,"E50.top")])],"isStart":false});
            var Q19;
            Q19=makeQuery(id+"F4.opExtrude","CAP_EDGE",EDGE,{"disambiguationData":[OSD([sQuery(id+"F0.wireOp",EDGE,"E49.top")])],"isStart":false});
            var Q20;
            Q20=makeQuery(id+"F1.opExtrude","CAP_EDGE",EDGE,{"disambiguationData":[OSD([sQuery(id+"F0.wireOp",EDGE,"E50.top")])],"isStart":false});
            var Q21;
            Q21=makeQuery(id+"F1.opExtrude","CAP_EDGE",EDGE,{"disambiguationData":[OSD([sQuery(id+"F0.wireOp",EDGE,"E49.top")])],"isStart":false});
            fillet(context, id + "F11", {"entities" : qUnion([Q0, Q1, Q2, Q3, Q4, Q5, Q6, Q7, Q8, Q9, Q10, Q11, Q12, Q13, Q14, Q15, Q16, Q17, Q18, Q19, Q20, Q21]), "radius" : 3.5 * mm, "tangentPropagation" : true, "allowEdgeOverflow" : false});
        }
        {
            var Q0;
            Q0=makeQuery(id+"F11.opFillet","SPLIT",FACE,{"disambiguationData":[OD(0.0)],"derivedFrom":makeQuery(id+"F4.opExtrude","CAP_FACE",FACE,{"disambiguationData":[OSD([sQuery(id+"F0.wireOp",EDGE,"E0"),sQuery(id+"F0.wireOp",EDGE,"E2"),sQuery(id+"F0.wireOp",EDGE,"E3"),sQuery(id+"F0.wireOp",EDGE,"E4.top"),sQuery(id+"F0.wireOp",EDGE,"E4.left"),sQuery(id+"F0.wireOp",EDGE,"E4.right"),sQuery(id+"F0.wireOp",EDGE,"E5.top"),sQuery(id+"F0.wireOp",EDGE,"E5.left"),sQuery(id+"F0.wireOp",EDGE,"E5.right"),sQuery(id+"F0.wireOp",EDGE,"E6.bottom"),sQuery(id+"F0.wireOp",EDGE,"E6.left"),sQuery(id+"F0.wireOp",EDGE,"E6.right"),sQuery(id+"F0.wireOp",EDGE,"E7.bottom"),sQuery(id+"F0.wireOp",EDGE,"E7.left"),sQuery(id+"F0.wireOp",EDGE,"E8.right"),sQuery(id+"F0.wireOp",EDGE,"E9.bottom"),sQuery(id+"F0.wireOp",EDGE,"E9.left"),sQuery(id+"F0.wireOp",EDGE,"E9.right"),sQuery(id+"F0.wireOp",EDGE,"E10.top"),sQuery(id+"F0.wireOp",EDGE,"E10.left"),sQuery(id+"F0.wireOp",EDGE,"E10.right"),sQuery(id+"F0.wireOp",EDGE,"E11.top"),sQuery(id+"F0.wireOp",EDGE,"E11.left"),sQuery(id+"F0.wireOp",EDGE,"E12"),sQuery(id+"F0.wireOp",EDGE,"E13.top"),sQuery(id+"F0.wireOp",EDGE,"E13.left"),sQuery(id+"F0.wireOp",EDGE,"E14.bottom"),sQuery(id+"F0.wireOp",EDGE,"E14.left"),sQuery(id+"F0.wireOp",EDGE,"E14.right"),sQuery(id+"F0.wireOp",EDGE,"E15"),sQuery(id+"F0.wireOp",EDGE,"E16"),sQuery(id+"F0.wireOp",EDGE,"E17"),sQuery(id+"F0.wireOp",EDGE,"E18"),sQuery(id+"F0.wireOp",EDGE,"E19"),sQuery(id+"F0.wireOp",EDGE,"E20"),sQuery(id+"F0.wireOp",EDGE,"E21"),sQuery(id+"F0.wireOp",EDGE,"E22"),sQuery(id+"F0.wireOp",EDGE,"E23"),sQuery(id+"F0.wireOp",EDGE,"E24"),sQuery(id+"F0.wireOp",EDGE,"E25"),sQuery(id+"F0.wireOp",EDGE,"E26"),sQuery(id+"F0.wireOp",EDGE,"E35"),sQuery(id+"F0.wireOp",EDGE,"E36"),sQuery(id+"F0.wireOp",EDGE,"E37"),sQuery(id+"F0.wireOp",EDGE,"E38"),sQuery(id+"F0.wireOp",EDGE,"E39"),sQuery(id+"F0.wireOp",EDGE,"E40"),sQuery(id+"F0.wireOp",EDGE,"E41"),sQuery(id+"F0.wireOp",EDGE,"E42"),sQuery(id+"F0.wireOp",EDGE,"E43"),sQuery(id+"F0.wireOp",EDGE,"E44"),sQuery(id+"F0.wireOp",EDGE,"E46"),sQuery(id+"F0.wireOp",EDGE,"E47"),sQuery(id+"F0.wireOp",EDGE,"E48")])],"isStart":false})});
            var sketch = newSketch(context, id + "F12", { "sketchPlane" : qUnion([Q0])});
            skLineSegment(sketch, "E54.bottom", {"start": v(60.25, 6.5) * mm, "end": v(54.25, 6.5) * mm});
            skLineSegment(sketch, "E54.top", {"start": v(60.25, 16.67) * mm, "end": v(54.25, 16.67) * mm});
            skLineSegment(sketch, "E54.left", {"start": v(60.25, 6.5) * mm, "end": v(60.25, 16.67) * mm});
            skLineSegment(sketch, "E54.right", {"start": v(54.25, 6.5) * mm, "end": v(54.25, 16.67) * mm});
            skLineSegment(sketch, "E55.bottom", {"start": v(-55.75, 6.5) * mm, "end": v(-61.75, 6.5) * mm});
            skLineSegment(sketch, "E55.top", {"start": v(-55.75, 16.5) * mm, "end": v(-61.75, 16.5) * mm});
            skLineSegment(sketch, "E55.left", {"start": v(-55.75, 6.5) * mm, "end": v(-55.75, 16.5) * mm});
            skLineSegment(sketch, "E55.right", {"start": v(-61.75, 6.5) * mm, "end": v(-61.75, 16.5) * mm});
            skLineSegment(sketch, "E56.right", {"start": v(54.25, 6.5) * mm, "end": v(54.25, 16.5) * mm});
            skLineSegment(sketch, "E57.bottom", {"start": v(-33.75, 6.5) * mm, "end": v(-27.75, 6.5) * mm});
            skLineSegment(sketch, "E57.top", {"start": v(-33.75, 16.5) * mm, "end": v(-27.75, 16.5) * mm});
            skLineSegment(sketch, "E57.left", {"start": v(-33.75, 6.5) * mm, "end": v(-33.75, 16.5) * mm});
            skLineSegment(sketch, "E57.right", {"start": v(-27.75, 6.5) * mm, "end": v(-27.75, 16.5) * mm});
            skSolve(sketch);
        }
        {
            var Q0;
            Q0 = qSketchRegion(id + "F12", true);
            var Q1;
            Q1=makeQuery(id+"F4.opExtrude","CAP_EDGE",EDGE,{"disambiguationData":[OSD([sQuery(id+"F0.wireOp",EDGE,"E37")])],"isStart":false});
            revolve(context, id + "F13", {"operationType" : NewBodyOperationType.REMOVE, "surfaceOperationType" : NewSurfaceOperationType.NEW, "entities" : qUnion([Q0]), "axis" : qUnion([Q1]), "revolveType" : RevolveType.ONE_DIRECTION, "oppositeDirection" : true, "angle" : 57 * degree});
        }
        {
            var Q0;
            Q0=makeQuery(id+"F0.imprint","IMPRINT",FACE,{"disambiguationData":[TD([[makeQuery(id+"F0.imprint","IMPRINT",EDGE,{"derivedFrom":sQuery(id+"F0.wireOp",EDGE,"E0")}),-1.0]])]});
            extrude(context, id + "F14", {"entities" : qUnion([Q0]), "operationType" : NewBodyOperationType.ADD, "depth" : 14 * mm, "offsetDistance" : 25 * mm});
        }
        {
            var Q0;
            Q0=qCreatedBy(makeId("Front.planeOp"),FACE);
            cPlane(context, id + "F15", {"entities" : qUnion([Q0]), "cplaneType" : CPlaneType.OFFSET, "offset" : 17 * mm, "width" : 150 * mm, "height" : 150 * mm});
        }
        {
            var Q0;
            Q0=makeQuery(id+"F1.opExtrude","SWEPT_BODY",BODY,{"disambiguationData":[OSD([sQuery(id+"F0.wireOp",EDGE,"E0"),sQuery(id+"F0.wireOp",EDGE,"E2"),sQuery(id+"F0.wireOp",EDGE,"E3"),sQuery(id+"F0.wireOp",EDGE,"E4.top"),sQuery(id+"F0.wireOp",EDGE,"E4.left"),sQuery(id+"F0.wireOp",EDGE,"E4.right"),sQuery(id+"F0.wireOp",EDGE,"E5.top"),sQuery(id+"F0.wireOp",EDGE,"E5.left"),sQuery(id+"F0.wireOp",EDGE,"E5.right"),sQuery(id+"F0.wireOp",EDGE,"E6.bottom"),sQuery(id+"F0.wireOp",EDGE,"E6.left"),sQuery(id+"F0.wireOp",EDGE,"E6.right"),sQuery(id+"F0.wireOp",EDGE,"E7.bottom"),sQuery(id+"F0.wireOp",EDGE,"E7.left"),sQuery(id+"F0.wireOp",EDGE,"E8.right"),sQuery(id+"F0.wireOp",EDGE,"E9.bottom"),sQuery(id+"F0.wireOp",EDGE,"E9.left"),sQuery(id+"F0.wireOp",EDGE,"E9.right"),sQuery(id+"F0.wireOp",EDGE,"E10.top"),sQuery(id+"F0.wireOp",EDGE,"E10.left"),sQuery(id+"F0.wireOp",EDGE,"E10.right"),sQuery(id+"F0.wireOp",EDGE,"E11.top"),sQuery(id+"F0.wireOp",EDGE,"E11.left"),sQuery(id+"F0.wireOp",EDGE,"E12"),sQuery(id+"F0.wireOp",EDGE,"E13.top"),sQuery(id+"F0.wireOp",EDGE,"E13.left"),sQuery(id+"F0.wireOp",EDGE,"E14.bottom"),sQuery(id+"F0.wireOp",EDGE,"E14.left"),sQuery(id+"F0.wireOp",EDGE,"E14.right"),sQuery(id+"F0.wireOp",EDGE,"E15"),sQuery(id+"F0.wireOp",EDGE,"E16"),sQuery(id+"F0.wireOp",EDGE,"E17"),sQuery(id+"F0.wireOp",EDGE,"E18"),sQuery(id+"F0.wireOp",EDGE,"E19"),sQuery(id+"F0.wireOp",EDGE,"E20"),sQuery(id+"F0.wireOp",EDGE,"E21"),sQuery(id+"F0.wireOp",EDGE,"E22"),sQuery(id+"F0.wireOp",EDGE,"E23"),sQuery(id+"F0.wireOp",EDGE,"E24"),sQuery(id+"F0.wireOp",EDGE,"E25"),sQuery(id+"F0.wireOp",EDGE,"E26"),sQuery(id+"F0.wireOp",EDGE,"E49.top"),sQuery(id+"F0.wireOp",EDGE,"E49.left"),sQuery(id+"F0.wireOp",EDGE,"E49.right"),sQuery(id+"F0.wireOp",EDGE,"E50.top"),sQuery(id+"F0.wireOp",EDGE,"E50.left"),sQuery(id+"F0.wireOp",EDGE,"E50.right")])]});
            var Q1;
            Q1=qCreatedBy(id+"F15.planeOp",FACE);
            mirror(context, id + "F16", {"entities" : qUnion([Q0]), "mirrorPlane" : qUnion([Q1])});
        }
    });
